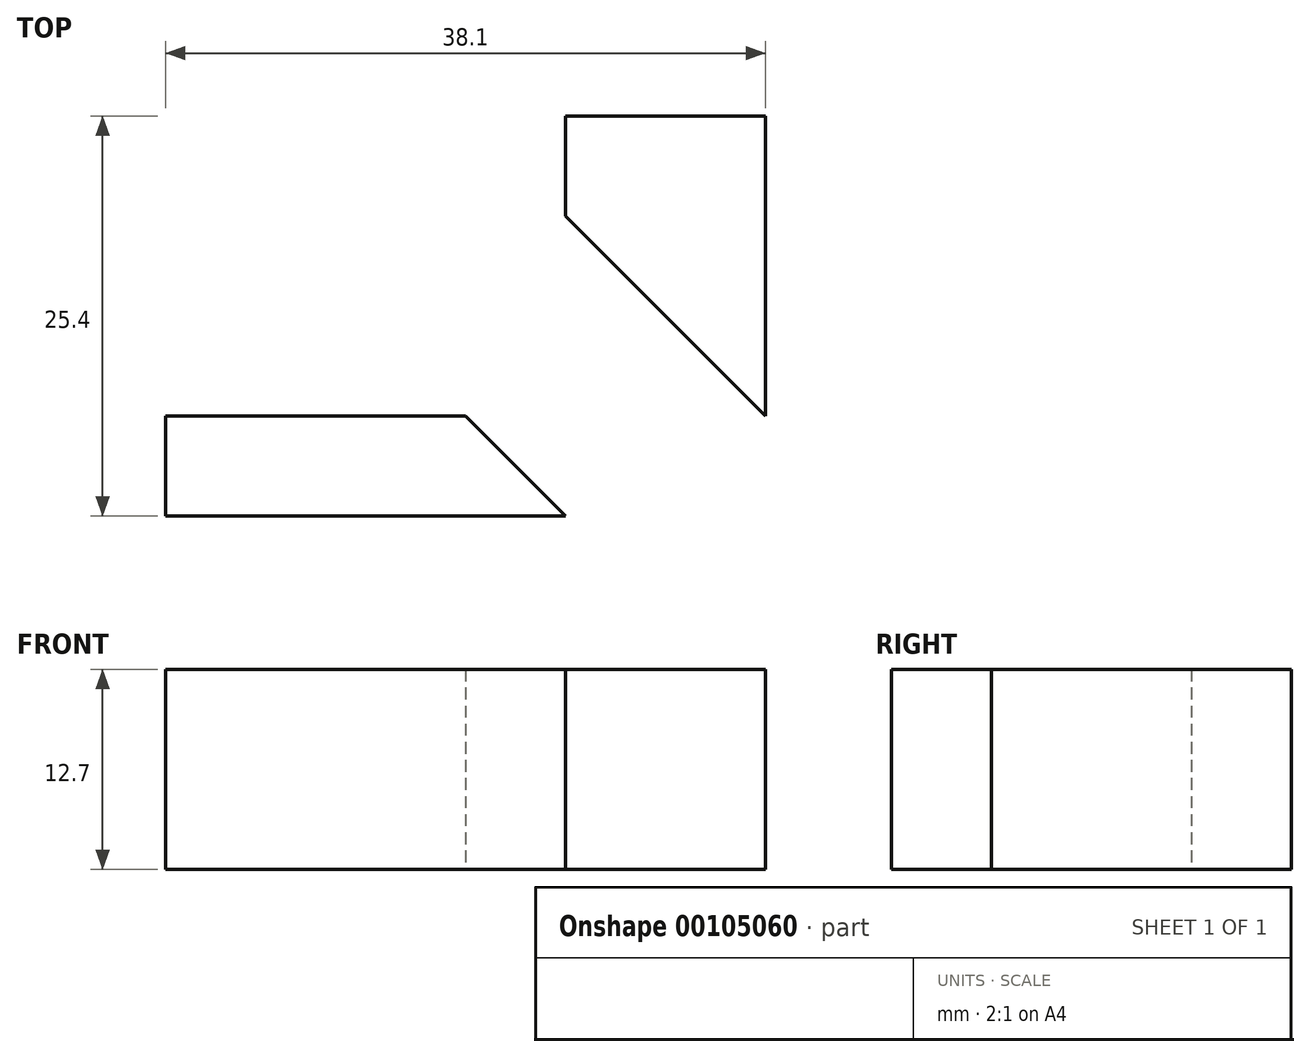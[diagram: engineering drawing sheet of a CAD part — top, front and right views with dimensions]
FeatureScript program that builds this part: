
annotation { "Feature Type Name" : "Feature", "Feature Type Description" : "" }
export const myFeature = defineFeature(function(context is Context, id is Id, definition is map)
    precondition{}
    {
        {
            var Q0;
            Q0=qCreatedBy(makeId("Front.planeOp"),FACE);
            var sketch = newSketch(context, id + "F0", { "sketchPlane" : qUnion([Q0])});
            skLineSegment(sketch, "E0.bottom", {"start": v(0, 0) * mm, "end": v(-38.1, 0) * mm});
            skLineSegment(sketch, "E0.top", {"start": v(0, -25.4) * mm, "end": v(-38.1, -25.4) * mm});
            skLineSegment(sketch, "E0.left", {"start": v(0, 0) * mm, "end": v(0, -25.4) * mm});
            skLineSegment(sketch, "E0.right", {"start": v(-38.1, 0) * mm, "end": v(-38.1, -25.4) * mm});
            skLineSegment(sketch, "E1.bottom", {"start": v(0, 0) * mm, "end": v(-12.7, 0) * mm});
            skLineSegment(sketch, "E1.top", {"start": v(0, -12.7) * mm, "end": v(-12.7, -12.7) * mm});
            skLineSegment(sketch, "E1.left", {"start": v(0, 0) * mm, "end": v(0, -12.7) * mm});
            skLineSegment(sketch, "E1.right", {"start": v(-12.7, 0) * mm, "end": v(-12.7, -12.7) * mm});
            skSolve(sketch);
        }
        {
            var Q0;
            Q0=qCreatedBy(makeId("Right.planeOp"),FACE);
            var sketch = newSketch(context, id + "F1", { "sketchPlane" : qUnion([Q0])});
            skLineSegment(sketch, "E2.bottom", {"start": v(0, 0) * mm, "end": v(25.4, 0) * mm});
            skLineSegment(sketch, "E2.top", {"start": v(0, -25.4) * mm, "end": v(25.4, -25.4) * mm});
            skLineSegment(sketch, "E2.left", {"start": v(0, 0) * mm, "end": v(0, -25.4) * mm});
            skLineSegment(sketch, "E2.right", {"start": v(25.4, 0) * mm, "end": v(25.4, -25.4) * mm});
            skLineSegment(sketch, "E3.bottom", {"start": v(0, 0) * mm, "end": v(6.35, 0) * mm});
            skLineSegment(sketch, "E3.top", {"start": v(0, -12.7) * mm, "end": v(6.35, -12.7) * mm});
            skLineSegment(sketch, "E3.left", {"start": v(0, 0) * mm, "end": v(0, -12.7) * mm});
            skLineSegment(sketch, "E3.right", {"start": v(6.35, 0) * mm, "end": v(6.35, -12.7) * mm});
            skSolve(sketch);
        }
        {
            var Q0;
            Q0=qCreatedBy(makeId("Top.planeOp"),FACE);
            var sketch = newSketch(context, id + "F2", { "sketchPlane" : qUnion([Q0])});
            skLineSegment(sketch, "E4.bottom", {"start": v(0, 0) * mm, "end": v(-38.1, 0) * mm});
            skLineSegment(sketch, "E4.top", {"start": v(0, 25.4) * mm, "end": v(-38.1, 25.4) * mm});
            skLineSegment(sketch, "E4.left", {"start": v(0, 0) * mm, "end": v(0, 25.4) * mm});
            skLineSegment(sketch, "E4.right", {"start": v(-38.1, 0) * mm, "end": v(-38.1, 25.4) * mm});
            skLineSegment(sketch, "E5", {"start": v(-38.1, 25.4) * mm, "end": v(-12.7, 0) * mm});
            skLineSegment(sketch, "E6", {"start": v(-12.7, 0) * mm, "end": v(0, 0) * mm});
            skLineSegment(sketch, "E7", {"start": v(0, 0) * mm, "end": v(0, 6.35) * mm});
            skLineSegment(sketch, "E8", {"start": v(0, 6.35) * mm, "end": v(-19.05, 25.4) * mm});
            skSolve(sketch);
        }
        {
            var Q0;
            Q0=makeQuery(id+"F1.imprint","IMPRINT",FACE,{"disambiguationData":[TD([[makeQuery(id+"F1.imprint","IMPRINT",EDGE,{"derivedFrom":sQuery(id+"F1.wireOp",EDGE,"E2.bottom")}),-1.0]])]});
            extrude(context, id + "F3", {"entities" : qUnion([Q0]), "oppositeDirection" : true, "depth" : 38.1 * mm});
        }
        {
            var Q0;
            Q0=makeQuery(id+"F0.imprint","IMPRINT",FACE,{"disambiguationData":[TD([[makeQuery(id+"F0.imprint","IMPRINT",EDGE,{"derivedFrom":sQuery(id+"F0.wireOp",EDGE,"E0.bottom")}),1.0]])]});
            extrude(context, id + "F4", {"entities" : qUnion([Q0]), "operationType" : NewBodyOperationType.ADD, "oppositeDirection" : true, "depth" : 25.4 * mm});
        }
        {
            var Q0;
            {var subQ1=sQuery(id+"F2.wireOp",EDGE,"E5");Q0=makeQuery(id+"F2.imprint","IMPRINT",FACE,{"disambiguationData":[TD([[makeQuery(id+"F2.imprint","IMPRINT",EDGE,{"derivedFrom":subQ1}),1.0]])]});}
            extrude(context, id + "F5", {"entities" : qUnion([Q0]), "operationType" : NewBodyOperationType.REMOVE, "oppositeDirection" : true, "depth" : 12.7 * mm});
        }
    });
